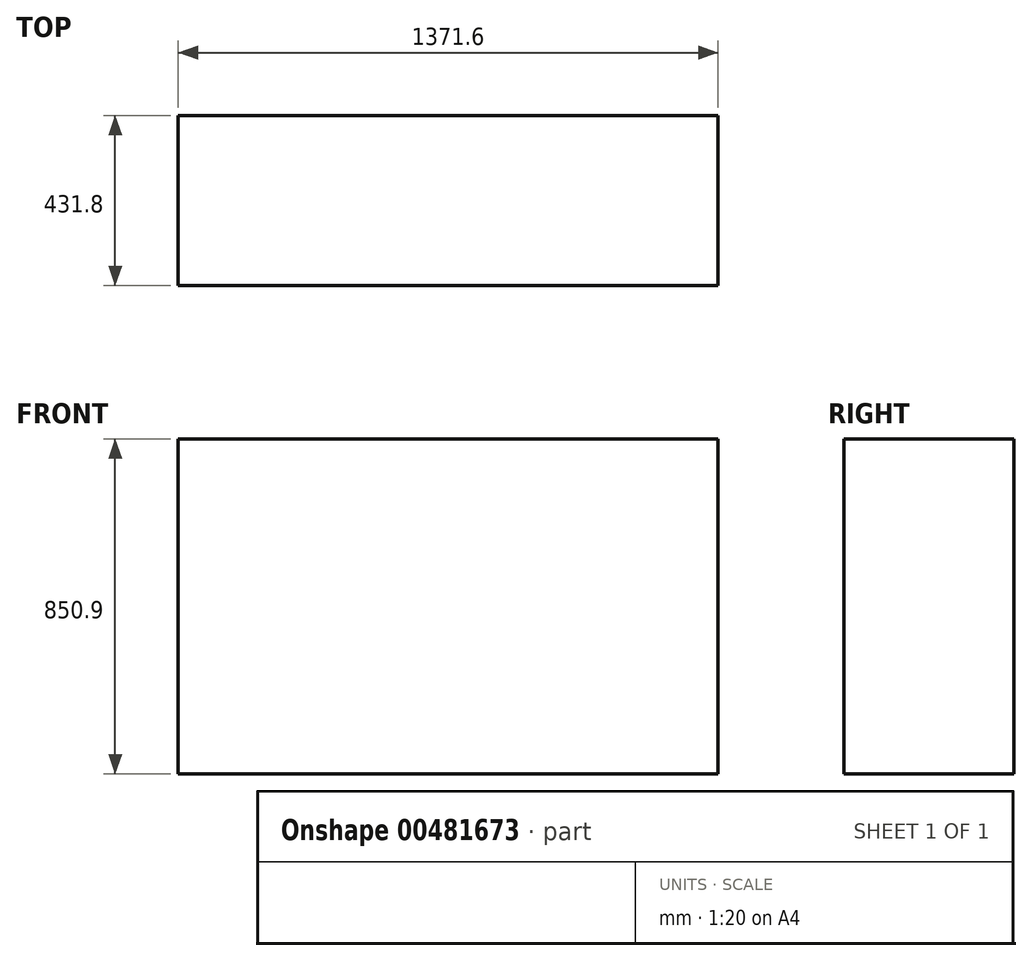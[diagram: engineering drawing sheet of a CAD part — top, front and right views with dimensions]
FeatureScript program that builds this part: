
annotation { "Feature Type Name" : "Feature", "Feature Type Description" : "" }
export const myFeature = defineFeature(function(context is Context, id is Id, definition is map)
    precondition{}
    {
        {
            var Q0;
            Q0=qCreatedBy(makeId("Top.planeOp"),FACE);
            var sketch = newSketch(context, id + "F0", { "sketchPlane" : qUnion([Q0])});
            skLineSegment(sketch, "E0.bottom", {"start": v(685.8, -215.9) * mm, "end": v(-685.8, -215.9) * mm});
            skLineSegment(sketch, "E0.top", {"start": v(685.8, 215.9) * mm, "end": v(-685.8, 215.9) * mm});
            skLineSegment(sketch, "E0.left", {"start": v(685.8, -215.9) * mm, "end": v(685.8, 215.9) * mm});
            skLineSegment(sketch, "E0.right", {"start": v(-685.8, -215.9) * mm, "end": v(-685.8, 215.9) * mm});
            skPoint(sketch, "E0.middle", {"position": v(0, 0) * mm});
            skSolve(sketch);
        }
        {
            var Q0;
            Q0 = qSketchRegion(id + "F0", true);
            extrude(context, id + "F1", {"entities" : qUnion([Q0]), "oppositeDirection" : true, "depth" : 850.9 * mm});
        }
    });
